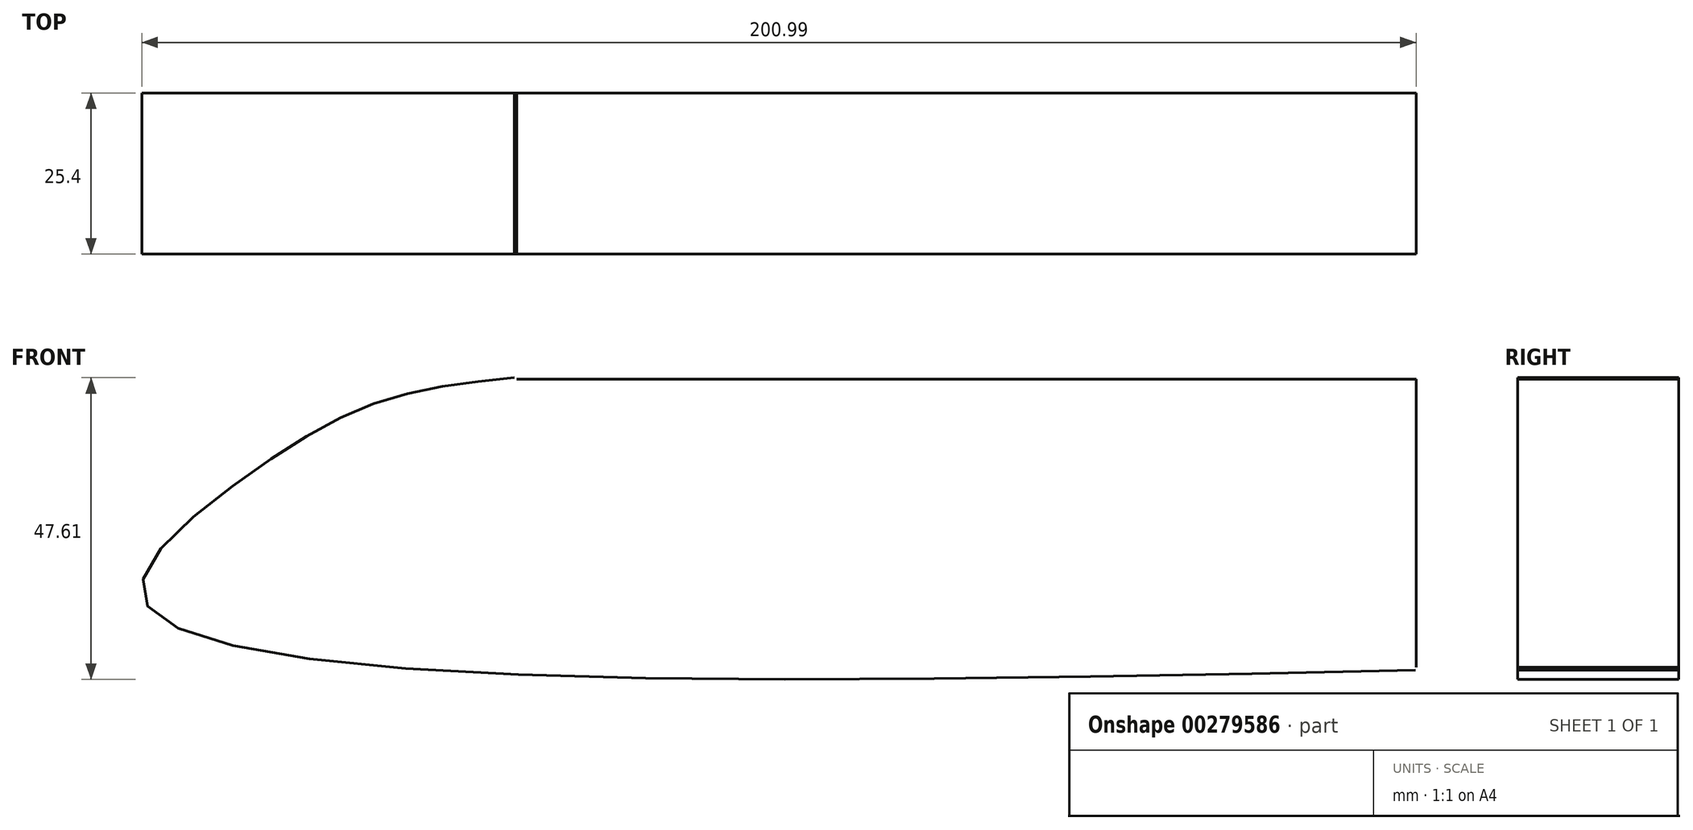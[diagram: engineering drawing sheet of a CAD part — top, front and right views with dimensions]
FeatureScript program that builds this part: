
annotation { "Feature Type Name" : "Feature", "Feature Type Description" : "" }
export const myFeature = defineFeature(function(context is Context, id is Id, definition is map)
    precondition{}
    {
        {
            var Q0;
            Q0=qCreatedBy(makeId("Front.planeOp"),FACE);
            var sketch = newSketch(context, id + "F0", { "sketchPlane" : qUnion([Q0])});
            skFitSpline(sketch, "E0", {"points": [v(-15.15, 38) * mm, v(-35.36, 34.55) * mm, v(-57.17, 22.61) * mm, v(-73.7, 3.33) * mm, v(126.97, -8.15) * mm], "startDerivative": vector(-131.12, -13.33) * mm, "endDerivative": vector(595.03, 12.84) * mm});
            skSolve(sketch);
        }
        {
            var Q0;
            Q0=qCreatedBy(makeId("Front.planeOp"),FACE);
            var sketch = newSketch(context, id + "F1", { "sketchPlane" : qUnion([Q0])});
            skLineSegment(sketch, "E1", {"start": v(-14.8, 37.77) * mm, "end": v(127.1, 37.77) * mm});
            skLineSegment(sketch, "E2", {"start": v(127.1, 37.77) * mm, "end": v(127.1, -7.7) * mm});
            skSolve(sketch);
        }
        {
            var Q0;
            Q0=sQuery(id+"F1.wireOp",EDGE,"E1");
            var Q1;
            Q1=sQuery(id+"F0.wireOp",EDGE,"E0");
            var Q2;
            Q2=sQuery(id+"F1.wireOp",EDGE,"E2");
            extrude(context, id + "F2", {"bodyType" : ToolBodyType.SURFACE, "surfaceEntities" : qUnion([Q0, Q1, Q2]), "depth" : 25.4 * mm});
        }
    });
